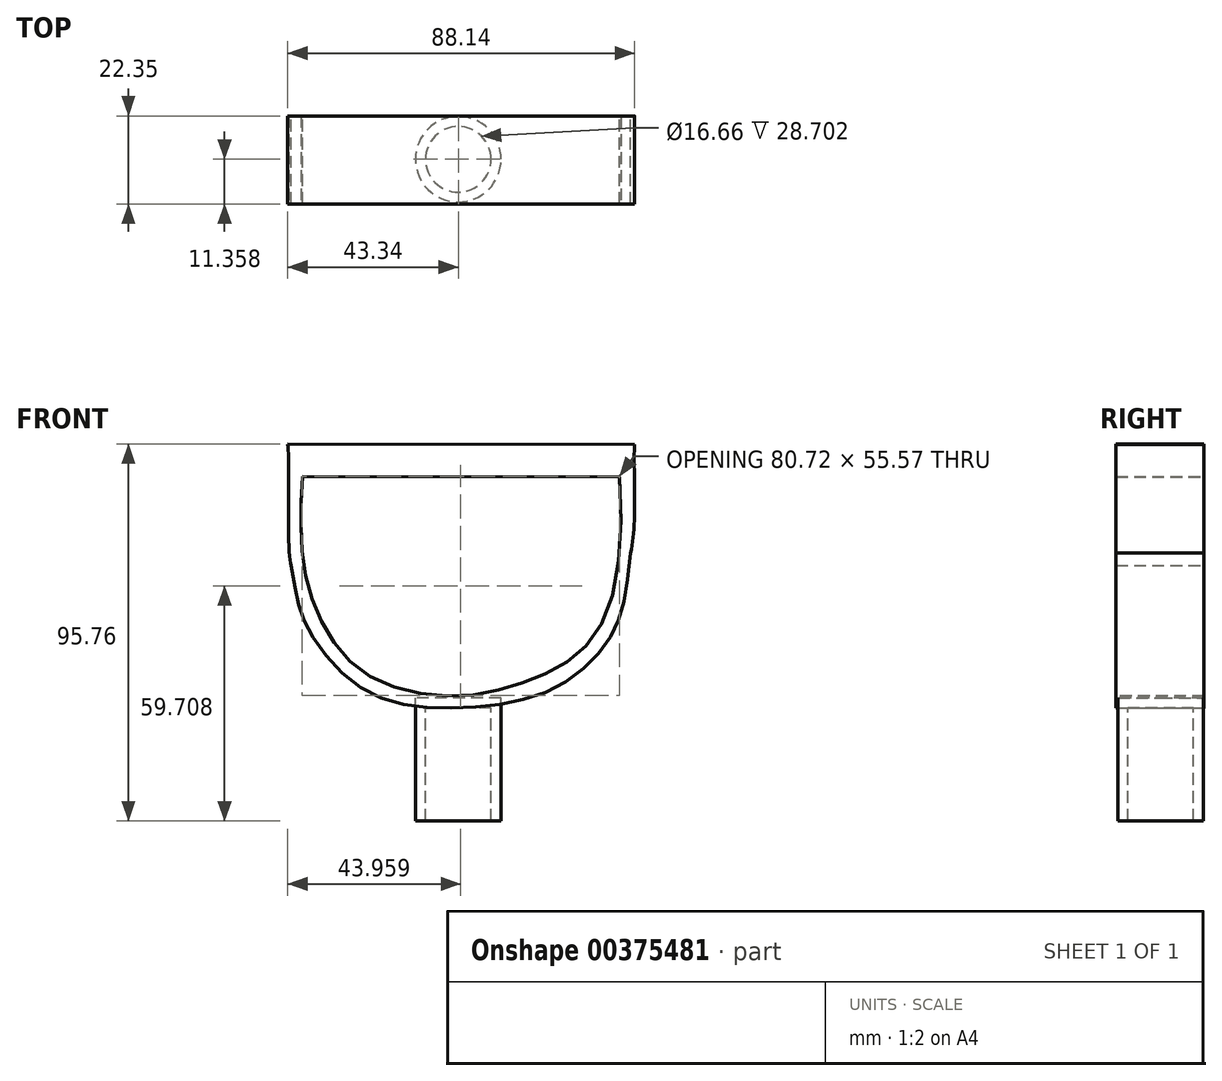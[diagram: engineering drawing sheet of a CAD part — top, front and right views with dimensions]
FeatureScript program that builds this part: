
annotation { "Feature Type Name" : "Feature", "Feature Type Description" : "" }
export const myFeature = defineFeature(function(context is Context, id is Id, definition is map)
    precondition{}
    {
        {
            var Q0;
            Q0=qCreatedBy(makeId("Front.planeOp"),FACE);
            var sketch = newSketch(context, id + "F0", { "sketchPlane" : qUnion([Q0])});
            skFitSpline(sketch, "E0", {"points": [v(-42.44, 36.16) * mm, v(-43.34, 67.06) * mm], "startDerivative": vector(-4.03, 12.69) * mm, "endDerivative": vector(-1.93, 12.97) * mm});
            skLineSegment(sketch, "E1", {"start": v(-43.34, 67.06) * mm, "end": v(44.74, 66.89) * mm});
            skLineSegment(sketch, "E2", {"start": v(-39.62, 58.8) * mm, "end": v(40.98, 58.63) * mm});
            skFitSpline(sketch, "E3", {"points": [v(-42.44, 36.16) * mm, v(-38.61, 21.1) * mm, v(-23.82, 4.55) * mm, v(0, 0) * mm, v(24.54, 5.11) * mm, v(39.04, 18.76) * mm, v(43.72, 39.44) * mm], "startDerivative": vector(26.22, -146.92) * mm, "endDerivative": vector(14.8, 175.7) * mm});
            skFitSpline(sketch, "E4", {"points": [v(-39.62, 58.8) * mm, v(-39.62, 39.37) * mm, v(-34.5, 21.47) * mm, v(-21.73, 7.67) * mm, v(0, 3.06) * mm, v(19.16, 7.43) * mm, v(34.82, 18.63) * mm, v(40.98, 58.63) * mm], "startDerivative": vector(-7.58, -148.64) * mm, "endDerivative": vector(-18.72, 267.88) * mm});
            skFitSpline(sketch, "E5", {"points": [v(43.72, 39.44) * mm, v(44.74, 66.89) * mm], "startDerivative": vector(5.37, 19.94) * mm, "endDerivative": vector(0.77, 29.65) * mm});
            skSolve(sketch);
        }
        {
            var Q0;
            Q0 = qSketchRegion(id + "F0", true);
            extrude(context, id + "F1", {"entities" : qUnion([Q0]), "depth" : 22.35 * mm});
        }
        {
            var Q0;
            Q0=qCreatedBy(makeId("Top.planeOp"),FACE);
            var sketch = newSketch(context, id + "F2", { "sketchPlane" : qUnion([Q0])});
            skCircle(sketch, "E6", {"center": v(0, -11) * mm, "radius": 8.33 * mm});
            skSolve(sketch);
        }
        {
            var Q0;
            Q0=makeQuery(id+"F2.imprint","IMPRINT",FACE,{"disambiguationData":[TD([[makeQuery(id+"F2.imprint","IMPRINT",EDGE,{"derivedFrom":sQuery(id+"F2.wireOp",EDGE,"E6")}),1.0]])]});
            extrude(context, id + "F3", {"entities" : qUnion([Q0]), "oppositeDirection" : true, "depth" : 28.7 * mm});
        }
        {
            var Q0;
            Q0=makeQuery(id+"F3.opExtrude","CAP_FACE",FACE,{"disambiguationData":[OSD([sQuery(id+"F2.wireOp",EDGE,"E6")])],"isStart":false});
            shell(context, id + "F4", {"entities" : qUnion([Q0]), "thickness" : 2.54 * mm, "oppositeDirection" : true});
        }
    });
